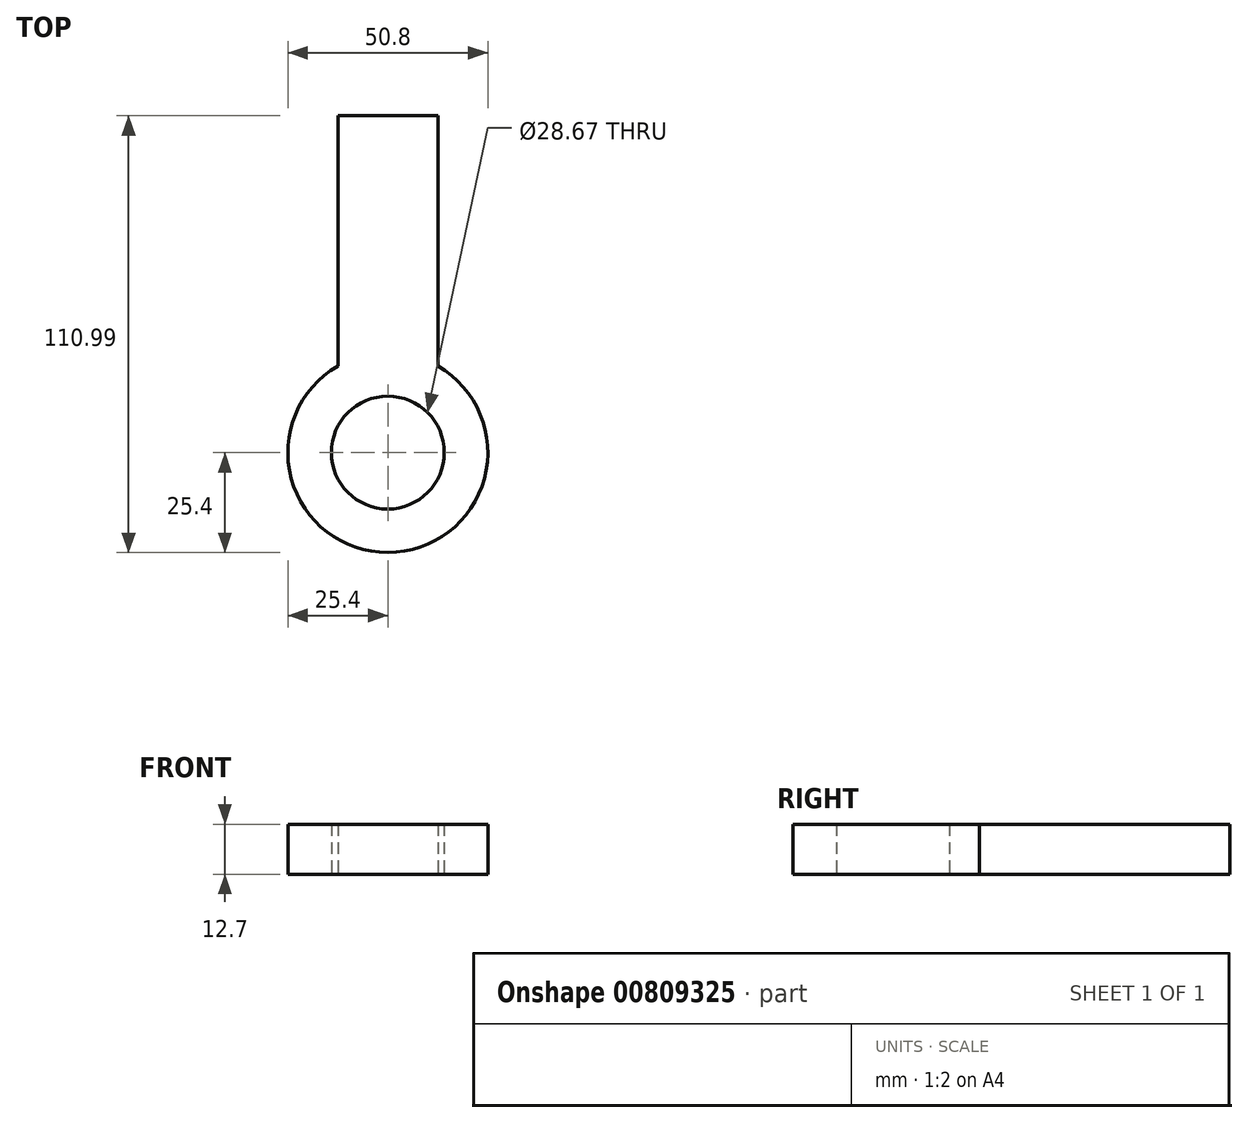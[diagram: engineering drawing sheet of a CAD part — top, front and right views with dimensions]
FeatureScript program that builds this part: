
annotation { "Feature Type Name" : "Feature", "Feature Type Description" : "" }
export const myFeature = defineFeature(function(context is Context, id is Id, definition is map)
    precondition{}
    {
        {
            var Q0;
            Q0=qCreatedBy(makeId("Top.planeOp"),FACE);
            var sketch = newSketch(context, id + "F0", { "sketchPlane" : qUnion([Q0])});
            skCircle(sketch, "E0", {"center": v(0, 0) * mm, "radius": 25.4 * mm});
            skPoint(sketch, "E1", {"position": v(0, 25.4) * mm});
            skPoint(sketch, "E2", {"position": v(-25.4, 0) * mm});
            skPoint(sketch, "E3", {"position": v(25.4, 0) * mm});
            skPoint(sketch, "E4", {"position": v(25.4, 25.4) * mm});
            skPoint(sketch, "E5", {"position": v(-25.4, 25.4) * mm});
            skPoint(sketch, "E6", {"position": v(-12.7, 25.4) * mm});
            skPoint(sketch, "E7", {"position": v(12.7, 25.4) * mm});
            skPoint(sketch, "E8", {"position": v(-12.7, 22) * mm});
            skPoint(sketch, "E9", {"position": v(12.7, 22) * mm});
            skLineSegment(sketch, "E10", {"start": v(-12.7, 22) * mm, "end": v(-12.7, 85.6) * mm});
            skLineSegment(sketch, "E11", {"start": v(-12.7, 85.6) * mm, "end": v(0, 85.6) * mm});
            skLineSegment(sketch, "E12", {"start": v(0, 85.6) * mm, "end": v(12.7, 85.6) * mm});
            skLineSegment(sketch, "E13", {"start": v(12.7, 85.6) * mm, "end": v(12.7, 22) * mm});
            skCircle(sketch, "E14", {"center": v(0, 0) * mm, "radius": 14.34 * mm});
            skSolve(sketch);
        }
        {
            var Q0;
            {var subQ0=sQuery(id+"F0.wireOp",EDGE,"E10");Q0=makeQuery(id+"F0.imprint","IMPRINT",FACE,{"disambiguationData":[TD([[makeQuery(id+"F0.imprint","IMPRINT",EDGE,{"derivedFrom":subQ0}),-1.0]])]});}
            var Q1;
            Q1=makeQuery(id+"F0.imprint","IMPRINT",FACE,{"disambiguationData":[TD([[makeQuery(id+"F0.imprint","IMPRINT",EDGE,{"derivedFrom":sQuery(id+"F0.wireOp",EDGE,"pBGBkjZO-6sIw-COvx-8Pyc-J7MczVylqA6r")}),-1.0]])]});
            var Q2;
            Q2=makeQuery(id+"F0.imprint","IMPRINT",FACE,{"disambiguationData":[TD([[makeQuery(id+"F0.imprint","IMPRINT",EDGE,{"derivedFrom":sQuery(id+"F0.wireOp",EDGE,"E14")}),-1.0]])]});
            extrude(context, id + "F1", {"entities" : qUnion([Q0, Q1, Q2]), "depth" : 12.7 * mm, "offsetDistance" : 25.4 * mm});
        }
    });
